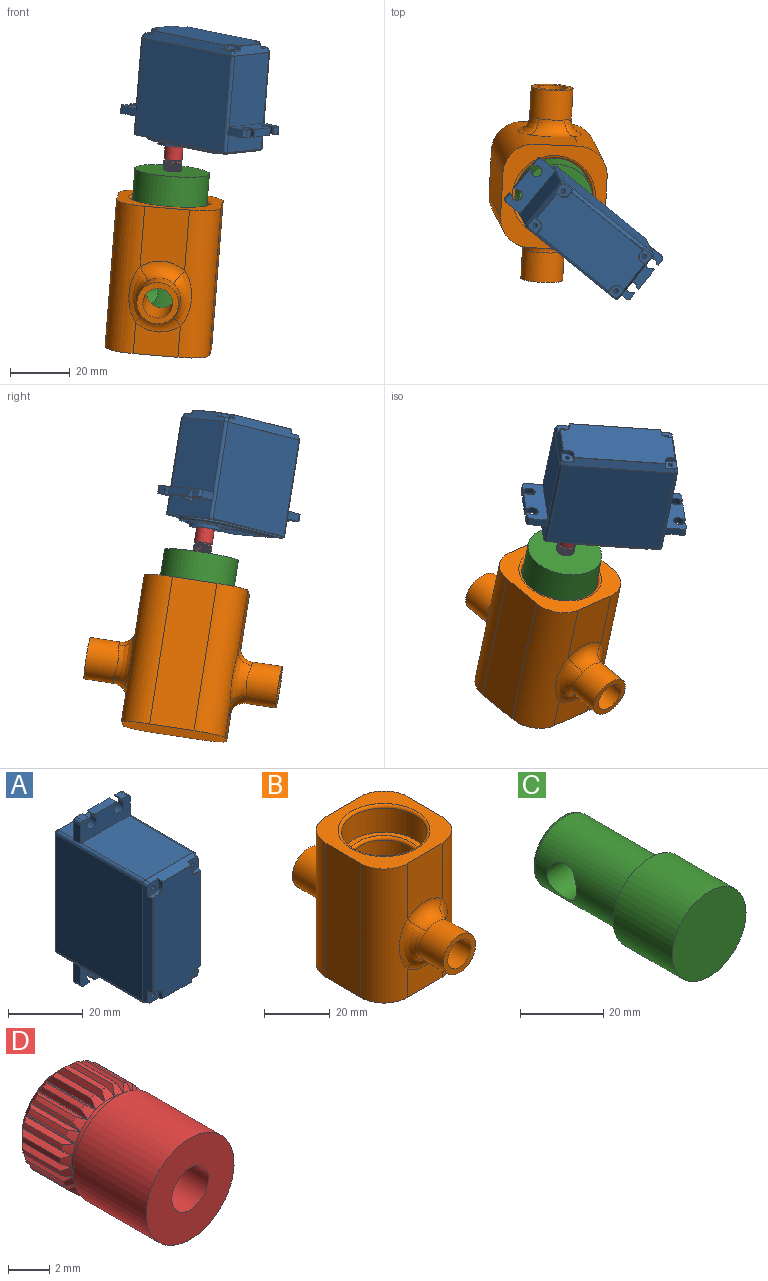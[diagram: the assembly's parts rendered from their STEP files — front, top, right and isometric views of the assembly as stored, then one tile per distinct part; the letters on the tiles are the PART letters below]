
ASSEMBLY  parts=4 mates=5
PART A: 161 faces, bbox 20.2x38.4x54.2 mm
  f0: plane 34.1x18.2mm, normal (0,1,0), area 228.8mm2, adj f139,f140,f141,f142,f143,f157,f158,f159
  f1: plane 13.5x13.5mm, normal (0,1,0), area 48.1mm2, adj f143,f144
  f2: plane 40x19.8mm, normal (0,1,0), area 85.3mm2, adj f132,f133,f134,f135,f136,f137,f148,f149
  f3: plane 8.78x7.07mm, normal (0,1,0), area 44.7mm2, adj f4,f7,f10,f54,f114,f117,f120,f121
  f4: plane 18x6.1mm, normal (0,0,1), area 108.6mm2, adj f3,f8,f54,f56,f129,f130,f131,f150
  f5: plane 8.78x7.07mm, normal (0,1,0), area 44.7mm2, adj f6,f15,f16,f53,f107,f109,f112,f113
  f6: plane 18x6.1mm, normal (0,0,-1), area 108.6mm2, adj f5,f13,f51,f53,f126,f127,f128,f153
  f7: plane 2.6x2.2mm, normal (0,0,1), area 5.7mm2, adj f3,f9,f117,f121
  f8: plane 8.78x7.07mm, normal (0,1,0), area 44.7mm2, adj f4,f10,f11,f56,f115,f116,f118,f119
  f9: plane 18.75x7.07mm, normal (0,-1,0), area 108.5mm2, adj f7,f10,f11,f12,f54,f56,f114,f115
  f10: plane 8.35x2.6mm, normal (0,0,1), area 21.7mm2, adj f3,f8,f9,f119,f120,f129
  f11: plane 2.6x2.2mm, normal (0,0,1), area 5.7mm2, adj f8,f9,f116,f118
  f12: plane 24.08x18mm, normal (0,0,1), area 433.5mm2, adj f9,f54,f56,f71
  f13: plane 8.78x7.07mm, normal (0,1,0), area 44.7mm2, adj f6,f15,f17,f51,f106,f108,f110,f111
  f14: plane 18.75x7.07mm, normal (0,-1,0), area 108.5mm2, adj f15,f16,f17,f18,f51,f53,f106,f107
  f15: plane 8.35x2.6mm, normal (0,0,-1), area 21.7mm2, adj f5,f13,f14,f110,f113,f126
  f16: plane 2.6x2.2mm, normal (0,0,-1), area 5.7mm2, adj f5,f14,f109,f112
  f17: plane 2.6x2.2mm, normal (0,0,-1), area 5.7mm2, adj f13,f14,f108,f111
  f18: plane 24.08x18mm, normal (0,0,-1), area 433.5mm2, adj f14,f51,f53,f60
  f19: plane 4.11x4.11mm, normal (0,-1,0), area 13.2mm2, adj f21,f22,f45,f46,f47,f48,f55,f92
  f20: plane 38.06x17.86mm, normal (0,-1,0), area 633.5mm2, adj f75,f79,f80,f81,f82,f84,f85,f90
  f21: plane 18.09x2.92mm, normal (0,-0.32,0.95), area 43.8mm2, adj f19,f30,f55,f57,f69,f71,f73,f86
  f22: plane 38.29x2.92mm, normal (0.95,-0.32,0), area 105.9mm2, adj f19,f41,f52,f55,f61,f63,f65,f99
  f23: plane 4.11x4.11mm, normal (0,-1,0), area 13.2mm2, adj f24,f25,f34,f35,f36,f37,f50,f74
  f24: plane 38.29x2.92mm, normal (-0.95,-0.32,0), area 105.9mm2, adj f23,f30,f50,f57,f66,f68,f70,f74
  f25: plane 18.09x2.92mm, normal (0,-0.32,-0.95), area 43.8mm2, adj f23,f41,f50,f52,f58,f60,f62,f83
  f26: plane 38.2x32.78mm, normal (1,0,0), area 1252.3mm2, adj f53,f54,f63,f149
  f27: plane 38.2x32.78mm, normal (-1,0,0), area 1252.3mm2, adj f51,f56,f68,f154
  f28: plane 1.89x1.4mm, normal (-1,0,0), area 2.3mm2, adj f30,f31,f85,f86
  f29: plane 1.89x1.4mm, normal (0,0,1), area 2.3mm2, adj f30,f31,f76,f80
  f30: plane 4.11x4.11mm, normal (0,-1,0), area 13.2mm2, adj f21,f24,f28,f29,f31,f32,f57,f76
  f31: cylinder r=2mm len=2mm, axis (0,1,0), area 4.4mm2, adj f28,f29,f30,f82
  f32: cylinder r=0.75mm len=30mm, axis (0,-1,0), area 141.4mm2, adj f30,f33
  f33: plane 1.5x1.5mm, normal (0,-1,0), area 1.8mm2, adj f32
  f34: plane 1.89x1.4mm, normal (0,0,-1), area 2.3mm2, adj f23,f36,f74,f79
  f35: plane 1.89x1.4mm, normal (-1,0,0), area 2.3mm2, adj f23,f36,f83,f84
  f36: cylinder r=2mm len=2mm, axis (0,1,0), area 4.4mm2, adj f23,f34,f35,f81
  f37: cylinder r=0.75mm len=30mm, axis (0,-1,0), area 141.4mm2, adj f23,f38
  f38: plane 1.5x1.5mm, normal (0,-1,0), area 1.8mm2, adj f37
  f39: plane 1.89x1.4mm, normal (1,0,0), area 2.3mm2, adj f41,f42,f89,f95
  f40: plane 1.89x1.4mm, normal (0,0,-1), area 2.3mm2, adj f41,f42,f99,f100
  f41: plane 4.11x4.11mm, normal (0,-1,0), area 13.2mm2, adj f22,f25,f39,f40,f42,f43,f52,f89
  f42: cylinder r=2mm len=2mm, axis (0,1,0), area 4.4mm2, adj f39,f40,f41,f97
  f43: cylinder r=0.75mm len=30mm, axis (0,-1,0), area 141.4mm2, adj f41,f44
  f44: plane 1.5x1.5mm, normal (0,-1,0), area 1.8mm2, adj f43
  f45: plane 1.89x1.4mm, normal (0,0,1), area 2.3mm2, adj f19,f47,f101,f102
  f46: plane 1.89x1.4mm, normal (1,0,0), area 2.3mm2, adj f19,f47,f92,f96
  f47: cylinder r=2mm len=2mm, axis (0,1,0), area 4.4mm2, adj f19,f45,f46,f98
  f48: cylinder r=0.75mm len=30mm, axis (0,-1,0), area 141.4mm2, adj f19,f49
  f49: plane 1.5x1.5mm, normal (0,-1,0), area 1.8mm2, adj f48
  f50: cylinder r=1mm len=1.64mm, axis (-0.3,0.9,-0.3), area 2.3mm2, adj f23,f24,f25,f64
  f51: cylinder r=1mm len=32.84mm, axis (0,-1,0), area 50.6mm2, adj f6,f13,f14,f18,f27,f62,f64,f66
  f52: cylinder r=1mm len=1.64mm, axis (-0.3,-0.9,0.3), area 2.3mm2, adj f22,f25,f41,f59
  f53: cylinder r=1mm len=32.84mm, axis (0,-1,0), area 50.6mm2, adj f5,f6,f14,f18,f26,f58,f59,f61
  f54: cylinder r=1mm len=32.84mm, axis (0,-1,0), area 50.6mm2, adj f3,f4,f9,f12,f26,f65,f67,f69
  f55: cylinder r=1mm len=1.64mm, axis (-0.3,-0.9,-0.3), area 2.3mm2, adj f19,f21,f22,f67
  f56: cylinder r=1mm len=32.84mm, axis (0,-1,0), area 50.6mm2, adj f4,f8,f9,f12,f27,f70,f72,f73
  f57: cylinder r=1mm len=1.64mm, axis (-0.3,0.9,0.3), area 2.3mm2, adj f21,f24,f30,f72
  f58: bspline ~0.22x0.07mm, area 0mm2, adj f25,f53,f59,f60
  f59: bspline ~1.04x1.04mm, area 0.1mm2, adj f52,f53,f58,f61
  f60: cylinder r=0.1mm len=18mm, axis (-1,0,0), area 0.6mm2, adj f18,f25,f58,f62
  f61: bspline ~0.35x0.07mm, area 0mm2, adj f22,f53,f59,f63
  f62: bspline ~0.35x0.07mm, area 0mm2, adj f25,f51,f60,f64
  f63: cylinder r=0.1mm len=38.2mm, axis (0,0,-1), area 1.2mm2, adj f22,f26,f61,f65
  f64: bspline ~1.04x1.04mm, area 0.1mm2, adj f50,f51,f62,f66
  f65: bspline ~0.22x0.07mm, area 0mm2, adj f22,f54,f63,f67
  f66: bspline ~0.22x0.07mm, area 0mm2, adj f24,f51,f64,f68
  f67: bspline ~1.04x1.04mm, area 0.1mm2, adj f54,f55,f65,f69
  f68: cylinder r=0.1mm len=38.2mm, axis (0,0,1), area 1.2mm2, adj f24,f27,f66,f70
  f69: bspline ~0.35x0.07mm, area 0mm2, adj f21,f54,f67,f71
  f70: bspline ~0.35x0.07mm, area 0mm2, adj f24,f56,f68,f72
  f71: cylinder r=0.1mm len=18mm, axis (1,0,0), area 0.6mm2, adj f12,f21,f69,f73
  f72: bspline ~1.04x1.04mm, area 0.1mm2, adj f56,f57,f70,f73
  f73: bspline ~0.22x0.07mm, area 0mm2, adj f21,f56,f71,f72
  f74: cylinder r=0.1mm len=1.46mm, axis (-0.32,0.95,0), area 0.2mm2, adj f23,f24,f34,f77
  f75: cylinder r=0.1mm len=31mm, axis (0,0,-1), area 3.9mm2, adj f20,f24,f77,f78
  f76: cylinder r=0.1mm len=1.46mm, axis (0.32,-0.95,0), area 0.2mm2, adj f24,f29,f30,f78
  f77: sphere r=0.1mm, area 0mm2, adj f74,f75,f79
  f78: sphere r=0.1mm, area 0mm2, adj f75,f76,f80
  f79: cylinder r=0.1mm len=1.43mm, axis (-1,0,0), area 0.2mm2, adj f20,f34,f77,f81
  f80: cylinder r=0.1mm len=1.43mm, axis (1,0,0), area 0.2mm2, adj f20,f29,f78,f82
  f81: torus R=2.1mm, axis (0,1,0), area 0.5mm2, adj f20,f36,f79,f84
  f82: torus R=2.1mm, axis (0,1,0), area 0.5mm2, adj f20,f31,f80,f85
  f83: cylinder r=0.1mm len=1.46mm, axis (0,-0.95,0.32), area 0.2mm2, adj f23,f25,f35,f87
  f84: cylinder r=0.1mm len=1.43mm, axis (0,0,1), area 0.2mm2, adj f20,f35,f81,f87
  f85: cylinder r=0.1mm len=1.43mm, axis (0,0,1), area 0.2mm2, adj f20,f28,f82,f88
  f86: cylinder r=0.1mm len=1.46mm, axis (0,0.95,0.32), area 0.2mm2, adj f21,f28,f30,f88
  f87: sphere r=0.1mm, area 0mm2, adj f83,f84,f90
  f88: sphere r=0.1mm, area 0mm2, adj f85,f86,f91
  f89: cylinder r=0.1mm len=1.46mm, axis (0,0.95,-0.32), area 0.2mm2, adj f25,f39,f41,f93
  f90: cylinder r=0.1mm len=10.8mm, axis (1,0,0), area 1.3mm2, adj f20,f25,f87,f93
  f91: cylinder r=0.1mm len=10.8mm, axis (-1,0,0), area 1.3mm2, adj f20,f21,f88,f94
  f92: cylinder r=0.1mm len=1.46mm, axis (0,-0.95,-0.32), area 0.2mm2, adj f19,f21,f46,f94
  f93: sphere r=0.1mm, area 0mm2, adj f89,f90,f95
  f94: sphere r=0.1mm, area 0mm2, adj f91,f92,f96
  f95: cylinder r=0.1mm len=1.43mm, axis (0,0,-1), area 0.2mm2, adj f20,f39,f93,f97
  f96: cylinder r=0.1mm len=1.43mm, axis (0,0,-1), area 0.2mm2, adj f20,f46,f94,f98
  f97: torus R=2.1mm, axis (0,1,0), area 0.5mm2, adj f20,f42,f95,f100
  f98: torus R=2.1mm, axis (0,1,0), area 0.5mm2, adj f20,f47,f96,f101
  f99: cylinder r=0.1mm len=1.46mm, axis (-0.32,-0.95,0), area 0.2mm2, adj f22,f40,f41,f103
  f100: cylinder r=0.1mm len=1.43mm, axis (-1,0,0), area 0.2mm2, adj f20,f40,f97,f103
  f101: cylinder r=0.1mm len=1.43mm, axis (1,0,0), area 0.2mm2, adj f20,f45,f98,f104
  f102: cylinder r=0.1mm len=1.46mm, axis (0.32,0.95,0), area 0.2mm2, adj f19,f22,f45,f104
  f103: sphere r=0.1mm, area 0mm2, adj f99,f100,f105
  f104: sphere r=0.1mm, area 0mm2, adj f101,f102,f105
  f105: cylinder r=0.1mm len=31mm, axis (0,0,1), area 3.9mm2, adj f20,f22,f103,f104
  f106: plane 6.07x2.6mm, normal (-1,0,0), area 15.8mm2, adj f13,f14,f51,f108
  f107: plane 6.07x2.6mm, normal (1,0,0), area 15.8mm2, adj f5,f14,f53,f109
  f108: cylinder r=1mm len=2.6mm, axis (0,-1,0), area 4.1mm2, adj f13,f14,f17,f106
  f109: cylinder r=1mm len=2.6mm, axis (0,-1,0), area 4.1mm2, adj f5,f14,f16,f107
  f110: plane 2.64x0.74mm, normal (-1,0,0), area 1.1mm2, adj f13,f14,f15,f122
  f111: plane 2.64x0.74mm, normal (1,0,0), area 1.1mm2, adj f13,f14,f17,f122
  f112: plane 2.64x0.74mm, normal (-1,0,0), area 1.1mm2, adj f5,f14,f16,f123
  f113: plane 2.64x0.74mm, normal (1,0,0), area 1.1mm2, adj f5,f14,f15,f123
  f114: plane 6.07x2.6mm, normal (1,0,0), area 15.8mm2, adj f3,f9,f54,f117
  f115: plane 6.07x2.6mm, normal (-1,0,0), area 15.8mm2, adj f8,f9,f56,f116
  f116: cylinder r=1mm len=2.6mm, axis (0,-1,0), area 4.1mm2, adj f8,f9,f11,f115
  f117: cylinder r=1mm len=2.6mm, axis (0,-1,0), area 4.1mm2, adj f3,f7,f9,f114
  f118: plane 2.64x0.74mm, normal (1,0,0), area 1.1mm2, adj f8,f9,f11,f124
  f119: plane 2.64x0.74mm, normal (-1,0,0), area 1.1mm2, adj f8,f9,f10,f124
  f120: plane 2.64x0.74mm, normal (1,0,0), area 1.1mm2, adj f3,f9,f10,f125
  f121: plane 2.64x0.74mm, normal (-1,0,0), area 1.1mm2, adj f3,f7,f9,f125
  f122: cone r=2.3mm half-angle=10.9deg, axis (0,1,0), area 28.5mm2, adj f13,f14,f110,f111
  f123: cone r=1.8mm half-angle=10.9deg, axis (0,1,0), area 28.5mm2, adj f5,f14,f112,f113
  f124: cone r=1.8mm half-angle=10.9deg, axis (0,1,0), area 28.5mm2, adj f8,f9,f118,f119
  f125: cone r=2.3mm half-angle=10.9deg, axis (0,1,0), area 28.5mm2, adj f3,f9,f120,f121
  f126: plane 7x1.2mm, normal (0,0.99,-0.14), area 8.5mm2, adj f6,f15,f127,f128
  f127: plane 7x1mm, normal (1,0,0), area 3.5mm2, adj f5,f6,f126
  f128: plane 7x1mm, normal (-1,0,0), area 3.5mm2, adj f6,f13,f126
  f129: plane 7x1.2mm, normal (0,0.99,0.14), area 8.5mm2, adj f4,f10,f130,f131
  f130: plane 7x1mm, normal (1,0,0), area 3.5mm2, adj f3,f4,f129
  f131: plane 7x1mm, normal (-1,0,0), area 3.5mm2, adj f4,f8,f129
  f132: cylinder r=9.5mm len=19mm, axis (0,-1,0), area 17.9mm2, adj f2,f133,f137,f140
  f133: plane 29.2x0.6mm, normal (-1,0,0), area 17.1mm2, adj f2,f132,f134,f138,f141,f142
  f134: cylinder r=0.5mm len=0.5mm, axis (0,-1,0), area 0.4mm2, adj f2,f133,f135,f138
  f135: plane 18x0.5mm, normal (0,0,1), area 9mm2, adj f2,f134,f136,f138
  f136: cylinder r=0.5mm len=0.5mm, axis (0,-1,0), area 0.4mm2, adj f2,f135,f137,f138
  f137: plane 29.2x0.6mm, normal (1,0,0), area 17.1mm2, adj f2,f132,f136,f138,f139,f142
  f138: plane 19x4.2mm, normal (0,1,0), area 79.7mm2, adj f133,f134,f135,f136,f137,f142
  f139: plane 25.4x0.4mm, normal (0.71,0.71,0), area 14.3mm2, adj f0,f137,f140,f142
  f140: cone r=9.1mm half-angle=45deg, axis (0,-1,0), area 16.5mm2, adj f0,f132,f139,f141
  f141: plane 25.4x0.4mm, normal (-0.71,0.71,0), area 14.3mm2, adj f0,f133,f140,f142
  f142: plane 19x0.5mm, normal (0,0.71,0.71), area 13.2mm2, adj f0,f133,f137,f138,f139,f141
  f143: cylinder r=6.75mm len=13.5mm, axis (0,-1,0), area 21.2mm2, adj f0,f1
  f144: cylinder r=5.5mm len=11mm, axis (0,-1,0), area 34.6mm2, adj f1,f145
  f145: plane 11x11mm, normal (0,1,0), area 64.8mm2, adj f144,f146
  f146: cylinder r=3.1mm len=6.2mm, axis (0,1,0), area 97.4mm2, adj f145,f147
  f147: plane 6.2x6.2mm, normal (0,1,0), area 30.2mm2, adj f146
  f148: torus R=0.9mm, axis (0,1,0), area 0.2mm2, adj f2,f54,f149,f150
  f149: cylinder r=0.1mm len=38.2mm, axis (0,0,1), area 6mm2, adj f2,f26,f148,f151
  f150: cylinder r=0.1mm len=18mm, axis (-1,0,0), area 2.8mm2, adj f2,f4,f148,f152
  f151: torus R=0.9mm, axis (0,1,0), area 0.2mm2, adj f2,f53,f149,f153
  f152: torus R=0.9mm, axis (0,1,0), area 0.2mm2, adj f2,f56,f150,f154
  f153: cylinder r=0.1mm len=18mm, axis (1,0,0), area 2.8mm2, adj f2,f6,f151,f155
  f154: cylinder r=0.1mm len=38.2mm, axis (0,0,-1), area 6mm2, adj f2,f27,f152,f155
  f155: torus R=0.9mm, axis (0,1,0), area 0.2mm2, adj f2,f51,f153,f154
  f156: plane 14.3x13.9mm, normal (0,1,0), area 198.8mm2, adj f157,f158,f159,f160
  f157: cylinder r=0.25mm len=14.4mm, axis (-1,0,0), area 5.6mm2, adj f0,f156,f158,f159
  f158: cylinder r=0.25mm len=14.8mm, axis (0,0,1), area 5.7mm2, adj f0,f156,f157,f160
  f159: cylinder r=0.25mm len=14.8mm, axis (0,0,-1), area 5.7mm2, adj f0,f156,f157,f160
  f160: cylinder r=0.25mm len=14.4mm, axis (1,0,0), area 5.6mm2, adj f0,f156,f158,f159
PART B: 32 faces, bbox 35x65x50 mm
  f0: plane 15x10.63mm, normal (0,1,0), area 132.5mm2, adj f4,f16,f17,f29
  f1: plane 20.63x15mm, normal (0,-1,0), area 282.5mm2, adj f7,f18,f19,f23
  f2: cylinder r=5mm len=23.55mm, axis (0,1,0), area 719.1mm2, adj f10,f21
  f3: plane 50x15mm, normal (-1,0,0), area 750mm2, adj f4,f7,f17,f19
  f4: plane 35x35mm, normal (0,0,-1), area 1139.2mm2, adj f0,f3,f5,f8,f16,f17,f18,f19
  f5: plane 50x15mm, normal (1,0,0), area 750mm2, adj f4,f7,f16,f18
  f6: cylinder r=5mm len=23.55mm, axis (0,1,0), area 719.1mm2, adj f10,f27
  f7: plane 35x35mm, normal (0,0,1), area 523.4mm2, adj f1,f3,f5,f9,f14,f16,f17,f18
  f8: plane 15x10.63mm, normal (0,-1,0), area 132.5mm2, adj f4,f18,f19,f24
  f9: plane 20.63x15mm, normal (0,1,0), area 282.5mm2, adj f7,f16,f17,f30
  f10: cylinder r=10.25mm len=29mm, axis (0,0,1), area 1705.6mm2, adj f2,f6,f11,f15
  f11: plane 20.5x20.5mm, normal (0,0,1), area 330.1mm2, adj f10
  f12: cylinder r=13mm len=26mm, axis (0,0,1), area 735.1mm2, adj f13,f14
  f13: plane 26x26mm, normal (0,0,1), area 133.3mm2, adj f12,f15
  f14: torus R=14mm, axis (0,0,1), area 131.9mm2, adj f7,f12
  f15: torus R=11.25mm, axis (0,0,1), area 104.7mm2, adj f10,f13
  f16: cylinder r=10mm len=50mm, axis (0,0,1), area 745.8mm2, adj f0,f4,f5,f7,f9,f28
  f17: cylinder r=10mm len=50mm, axis (0,0,-1), area 745.8mm2, adj f0,f3,f4,f7,f9,f31
  f18: cylinder r=10mm len=50mm, axis (0,0,-1), area 745.8mm2, adj f1,f4,f5,f7,f8,f22
  f19: cylinder r=10mm len=50mm, axis (0,0,1), area 745.8mm2, adj f1,f3,f4,f7,f8,f25
  f20: cylinder r=7mm len=14mm, axis (0,1,0), area 448.8mm2, adj f21,f22,f23,f24,f25
  f21: plane 14x14mm, normal (0,-1,0), area 75.4mm2, adj f2,f20
  f22: bspline ~20.34x7.22mm, area 104.7mm2, adj f18,f20,f23,f24
  f23: torus R=12mm, axis (0,-1,0), area 93.5mm2, adj f1,f20,f22,f25
  f24: torus R=12mm, axis (0,-1,0), area 93.5mm2, adj f8,f20,f22,f25
  f25: bspline ~20.34x7.22mm, area 104.7mm2, adj f19,f20,f23,f24
  f26: cylinder r=7mm len=14mm, axis (0,-1,0), area 448.8mm2, adj f27,f28,f29,f30,f31
  f27: plane 14x14mm, normal (0,1,0), area 75.4mm2, adj f6,f26
  f28: bspline ~20.34x7.22mm, area 104.7mm2, adj f16,f26,f29,f30
  f29: torus R=12mm, axis (0,-1,0), area 93.5mm2, adj f0,f26,f28,f31
  f30: torus R=12mm, axis (0,-1,0), area 93.5mm2, adj f9,f26,f28,f31
  f31: bspline ~20.34x7.22mm, area 104.7mm2, adj f17,f26,f29,f30
PART C: 7 faces, bbox 25x50x25 mm
  f0: cylinder r=12.5mm len=25mm, axis (0,1,0), area 1570.8mm2, adj f1,f3
  f1: plane 25x25mm, normal (0,-1,0), area 490.9mm2, adj f0
  f2: cylinder r=10mm len=29mm, axis (0,1,0), area 1659.9mm2, adj f3,f5,f6
  f3: plane 25x25mm, normal (0,1,0), area 176.7mm2, adj f0,f2
  f4: plane 18x18mm, normal (0,1,0), area 254.5mm2, adj f6
  f5: cylinder r=5mm len=20mm, axis (-1,0,0), area 587mm2, adj f2
  f6: torus R=9mm, axis (0,-1,0), area 95.1mm2, adj f2,f4
PART D: 108 faces, bbox 6x9x6 mm
  f0: cylinder r=3mm len=2.6mm, axis (0,-1,0), area 0.8mm2, adj f2,f3,f81,f82
  f1: cylinder r=3mm len=2.6mm, axis (0,-1,0), area 0.8mm2, adj f2,f3,f33,f83
  f2: cone r=2.5mm half-angle=45deg, axis (0,-1,0), area 9.1mm2, adj f0,f1,f4,f5,f6,f7,f8,f9
  f3: cone r=3mm half-angle=45deg, axis (0,1,0), area 6.9mm2, adj f0,f1,f4,f5,f6,f7,f8,f9
  f4: cylinder r=3mm len=2.6mm, axis (0,-1,0), area 0.8mm2, adj f2,f3,f79,f80
  f5: cylinder r=3mm len=2.6mm, axis (0,-1,0), area 0.8mm2, adj f2,f3,f77,f78
  f6: cylinder r=3mm len=2.6mm, axis (0,-1,0), area 0.8mm2, adj f2,f3,f75,f76
  f7: cylinder r=3mm len=2.6mm, axis (0,-1,0), area 0.8mm2, adj f2,f3,f73,f74
  f8: cylinder r=3mm len=2.6mm, axis (0,-1,0), area 0.8mm2, adj f2,f3,f71,f72
  f9: cylinder r=3mm len=2.6mm, axis (0,-1,0), area 0.8mm2, adj f2,f3,f69,f70
  f10: cylinder r=3mm len=2.6mm, axis (0,-1,0), area 0.8mm2, adj f2,f3,f67,f68
  f11: cylinder r=3mm len=2.6mm, axis (0,-1,0), area 0.8mm2, adj f2,f3,f65,f66
  f12: cylinder r=3mm len=2.6mm, axis (0,-1,0), area 0.8mm2, adj f2,f3,f63,f64
  f13: cylinder r=3mm len=2.6mm, axis (0,-1,0), area 0.8mm2, adj f2,f3,f61,f62
  f14: cylinder r=3mm len=2.6mm, axis (0,-1,0), area 0.8mm2, adj f2,f3,f59,f60
  f15: cylinder r=3mm len=2.6mm, axis (0,-1,0), area 0.8mm2, adj f2,f3,f57,f58
  f16: cylinder r=3mm len=2.6mm, axis (0,-1,0), area 0.8mm2, adj f2,f3,f55,f56
  f17: cylinder r=3mm len=2.6mm, axis (0,-1,0), area 0.8mm2, adj f2,f3,f53,f54
  f18: cylinder r=3mm len=2.6mm, axis (0,-1,0), area 0.8mm2, adj f2,f3,f51,f52
  f19: cylinder r=3mm len=2.6mm, axis (0,-1,0), area 0.8mm2, adj f2,f3,f49,f50
  f20: cylinder r=3mm len=2.6mm, axis (0,-1,0), area 0.8mm2, adj f2,f3,f47,f48
  f21: cylinder r=3mm len=2.6mm, axis (0,-1,0), area 0.8mm2, adj f2,f3,f45,f46
  f22: cylinder r=3mm len=2.6mm, axis (0,-1,0), area 0.8mm2, adj f2,f3,f43,f44
  f23: cylinder r=3mm len=2.6mm, axis (0,-1,0), area 0.8mm2, adj f2,f3,f41,f42
  f24: cylinder r=3mm len=2.6mm, axis (0,-1,0), area 0.8mm2, adj f2,f3,f39,f40
  f25: cylinder r=3mm len=2.6mm, axis (0,-1,0), area 0.8mm2, adj f2,f3,f37,f38
  f26: cylinder r=3mm len=2.6mm, axis (0,-1,0), area 0.8mm2, adj f2,f3,f34,f36
  f27: cylinder r=3mm len=6mm, axis (0,-1,0), area 94.2mm2, adj f28,f29
  f28: plane 6x6mm, normal (0,-1,0), area 23.4mm2, adj f27,f32
  f29: plane 6x6mm, normal (0,1,0), area 7mm2, adj f27,f30
  f30: cylinder r=2.6mm len=5.2mm, axis (0,1,0), area 8.2mm2, adj f3,f29
  f31: plane 5x5mm, normal (0,1,0), area 14.7mm2, adj f2,f32
  f32: cylinder r=1.25mm len=9mm, axis (0,1,0), area 70.7mm2, adj f28,f31
  f33: plane 3.33x0.36mm, normal (0.87,0,-0.5), area 1.2mm2, adj f1,f2,f3,f35
  f34: plane 3.33x0.36mm, normal (-0.87,0,-0.5), area 1.2mm2, adj f2,f3,f26,f35
  f35: plane 3.31x0.05mm, normal (0,0,-1), area 0.2mm2, adj f2,f3,f33,f34
  f36: plane 3.33x0.4mm, normal (0.96,0,-0.27), area 1.2mm2, adj f2,f3,f26,f84
  f37: plane 3.33x0.3mm, normal (-0.71,0,-0.7), area 1.2mm2, adj f2,f3,f25,f84
  f38: plane 3.33x0.41mm, normal (1,0,-0.02), area 1.2mm2, adj f2,f3,f25,f85
  f39: plane 3.33x0.36mm, normal (-0.52,0,-0.86), area 1.2mm2, adj f2,f3,f24,f85
  f40: plane 3.33x0.4mm, normal (0.97,0,0.23), area 1.2mm2, adj f2,f3,f24,f86
  f41: plane 3.33x0.4mm, normal (-0.29,0,-0.96), area 1.2mm2, adj f2,f3,f23,f86
  f42: plane 3.33x0.37mm, normal (0.89,0,0.46), area 1.2mm2, adj f2,f3,f23,f87
  f43: plane 3.33x0.41mm, normal (-0.04,0,-1), area 1.2mm2, adj f2,f3,f22,f87
  f44: plane 3.33x0.31mm, normal (0.74,0,0.67), area 1.2mm2, adj f2,f3,f22,f88
  f45: plane 3.33x0.41mm, normal (0.21,0,-0.98), area 1.2mm2, adj f2,f3,f21,f88
  f46: plane 3.33x0.35mm, normal (0.55,0,0.83), area 1.2mm2, adj f2,f3,f21,f89
  f47: plane 3.33x0.37mm, normal (0.44,0,-0.9), area 1.2mm2, adj f2,f3,f20,f89
  f48: plane 3.33x0.39mm, normal (0.33,0,0.94), area 1.2mm2, adj f2,f3,f20,f90
  f49: plane 3.33x0.32mm, normal (0.65,0,-0.76), area 1.2mm2, adj f2,f3,f19,f90
  f50: plane 3.33x0.41mm, normal (0.08,0,1), area 1.2mm2, adj f2,f3,f19,f91
  f51: plane 3.33x0.34mm, normal (0.82,0,-0.57), area 1.2mm2, adj f2,f3,f18,f91
  f52: plane 3.33x0.41mm, normal (-0.17,0,0.99), area 1.2mm2, adj f2,f3,f18,f92
  f53: plane 3.33x0.39mm, normal (0.94,0,-0.35), area 1.2mm2, adj f2,f3,f17,f92
  f54: plane 3.33x0.38mm, normal (-0.41,0,0.91), area 1.2mm2, adj f2,f3,f17,f93
  f55: plane 3.33x0.41mm, normal (0.99,0,-0.1), area 1.2mm2, adj f2,f3,f16,f93
  f56: plane 3.33x0.33mm, normal (-0.62,0,0.78), area 1.2mm2, adj f2,f3,f16,f94
  f57: plane 3.33x0.41mm, normal (0.99,0,0.15), area 1.2mm2, adj f2,f3,f15,f94
  f58: plane 3.33x0.33mm, normal (-0.8,0,0.6), area 1.2mm2, adj f2,f3,f15,f95
  f59: plane 3.33x0.38mm, normal (0.92,0,0.39), area 1.2mm2, adj f2,f3,f14,f95
  f60: plane 3.33x0.38mm, normal (-0.92,0,0.39), area 1.2mm2, adj f2,f3,f14,f96
  f61: plane 3.33x0.33mm, normal (0.8,0,0.6), area 1.2mm2, adj f2,f3,f13,f96
  f62: plane 3.33x0.41mm, normal (-0.99,0,0.15), area 1.2mm2, adj f2,f3,f13,f97
  f63: plane 3.33x0.33mm, normal (0.62,0,0.78), area 1.2mm2, adj f2,f3,f12,f97
  f64: plane 3.33x0.41mm, normal (-0.99,0,-0.1), area 1.2mm2, adj f2,f3,f12,f98
  f65: plane 3.33x0.38mm, normal (0.41,0,0.91), area 1.2mm2, adj f2,f3,f11,f98
  f66: plane 3.33x0.39mm, normal (-0.94,0,-0.35), area 1.2mm2, adj f2,f3,f11,f99
  f67: plane 3.33x0.41mm, normal (0.17,0,0.99), area 1.2mm2, adj f2,f3,f10,f99
  f68: plane 3.33x0.34mm, normal (-0.82,0,-0.57), area 1.2mm2, adj f2,f3,f10,f100
  f69: plane 3.33x0.41mm, normal (-0.08,0,1), area 1.2mm2, adj f2,f3,f9,f100
  f70: plane 3.33x0.32mm, normal (-0.65,0,-0.76), area 1.2mm2, adj f2,f3,f9,f101
  f71: plane 3.33x0.39mm, normal (-0.33,0,0.94), area 1.2mm2, adj f2,f3,f8,f101
  f72: plane 3.33x0.37mm, normal (-0.44,0,-0.9), area 1.2mm2, adj f2,f3,f8,f102
  f73: plane 3.33x0.35mm, normal (-0.55,0,0.83), area 1.2mm2, adj f2,f3,f7,f102
  f74: plane 3.33x0.41mm, normal (-0.21,0,-0.98), area 1.2mm2, adj f2,f3,f7,f103
  f75: plane 3.33x0.31mm, normal (-0.74,0,0.67), area 1.2mm2, adj f2,f3,f6,f103
  f76: plane 3.33x0.41mm, normal (0.04,0,-1), area 1.2mm2, adj f2,f3,f6,f104
  f77: plane 3.33x0.37mm, normal (-0.89,0,0.46), area 1.2mm2, adj f2,f3,f5,f104
  f78: plane 3.33x0.4mm, normal (0.29,0,-0.96), area 1.2mm2, adj f2,f3,f5,f105
  f79: plane 3.33x0.4mm, normal (-0.97,0,0.23), area 1.2mm2, adj f2,f3,f4,f105
  f80: plane 3.33x0.36mm, normal (0.52,0,-0.86), area 1.2mm2, adj f2,f3,f4,f106
  f81: plane 3.33x0.41mm, normal (-1,0,-0.02), area 1.2mm2, adj f0,f2,f3,f106
  f82: plane 3.33x0.3mm, normal (0.71,0,-0.7), area 1.2mm2, adj f0,f2,f3,f107
  f83: plane 3.33x0.4mm, normal (-0.96,0,-0.27), area 1.2mm2, adj f1,f2,f3,f107
  f84: plane 3.31x0.05mm, normal (0.25,0,-0.97), area 0.2mm2, adj f2,f3,f36,f37
  f85: plane 3.31x0.04mm, normal (0.48,0,-0.88), area 0.2mm2, adj f2,f3,f38,f39
  f86: plane 3.31x0.04mm, normal (0.68,0,-0.73), area 0.2mm2, adj f2,f3,f40,f41
  f87: plane 3.31x0.04mm, normal (0.84,0,-0.54), area 0.2mm2, adj f2,f3,f42,f43
  f88: plane 3.31x0.05mm, normal (0.95,0,-0.31), area 0.2mm2, adj f2,f3,f44,f45
  f89: plane 3.31x0.05mm, normal (1,0,-0.06), area 0.2mm2, adj f2,f3,f46,f47
  f90: plane 3.31x0.05mm, normal (0.98,0,0.19), area 0.2mm2, adj f2,f3,f48,f49
  f91: plane 3.31x0.05mm, normal (0.9,0,0.43), area 0.2mm2, adj f2,f3,f50,f51
  f92: plane 3.31x0.04mm, normal (0.77,0,0.64), area 0.2mm2, adj f2,f3,f52,f53
  f93: plane 3.31x0.04mm, normal (0.59,0,0.81), area 0.2mm2, adj f2,f3,f54,f55
  f94: plane 3.31x0.05mm, normal (0.37,0,0.93), area 0.2mm2, adj f2,f3,f56,f57
  f95: plane 3.31x0.05mm, normal (0.13,0,0.99), area 0.2mm2, adj f2,f3,f58,f59
  f96: plane 3.31x0.05mm, normal (-0.13,0,0.99), area 0.2mm2, adj f2,f3,f60,f61
  f97: plane 3.31x0.05mm, normal (-0.37,0,0.93), area 0.2mm2, adj f2,f3,f62,f63
  f98: plane 3.31x0.04mm, normal (-0.59,0,0.81), area 0.2mm2, adj f2,f3,f64,f65
  f99: plane 3.31x0.04mm, normal (-0.77,0,0.64), area 0.2mm2, adj f2,f3,f66,f67
  f100: plane 3.31x0.05mm, normal (-0.9,0,0.43), area 0.2mm2, adj f2,f3,f68,f69
  f101: plane 3.31x0.05mm, normal (-0.98,0,0.19), area 0.2mm2, adj f2,f3,f70,f71
  f102: plane 3.31x0.05mm, normal (-1,0,-0.06), area 0.2mm2, adj f2,f3,f72,f73
  f103: plane 3.31x0.05mm, normal (-0.95,0,-0.31), area 0.2mm2, adj f2,f3,f74,f75
  f104: plane 3.31x0.04mm, normal (-0.84,0,-0.54), area 0.2mm2, adj f2,f3,f76,f77
  f105: plane 3.31x0.04mm, normal (-0.68,0,-0.73), area 0.2mm2, adj f2,f3,f78,f79
  f106: plane 3.31x0.04mm, normal (-0.48,0,-0.88), area 0.2mm2, adj f2,f3,f80,f81
  f107: plane 3.31x0.05mm, normal (-0.25,0,-0.97), area 0.2mm2, adj f2,f3,f82,f83
PLACE A rot(axis=(-0.32,0.73,-0.6),145deg) t=(17.79,-4.9,-24.96)mm
PLACE B rot(axis=(0.85,0.45,-0.27),10.2deg) t=(5.6,29.28,-89.18)mm fixed
PLACE C rot(axis=(-0.8,-0.42,0.42),91.6deg) t=(-4.04,3.91,-102.52)mm
PLACE D rot(axis=(-0.32,0.73,-0.6),145deg) t=(8.44,4.49,-43.52)mm
MATE fastened D.f0 <-> A.f132  axis (0.08,-0.15,0.99) through (8.44,4.49,-43.52)mm
MATE planar B.f10 <-> C.f0  axis (0.08,-0.15,0.99) through (3.89,13.53,-101.65)mm
MATE cylindrical C.f0 <-> B.f10  axis (-0.08,0.15,-0.99) through (5.09,11.16,-86.38)mm
MATE fastened D.f0 <-> C.f0  axis (-0.08,0.15,-0.99) through (7.75,5.87,-52.39)mm
MATE cylindrical A.f132 <-> D.f0  axis (-0.08,0.15,-0.99) through (8.44,4.49,-43.52)mm
